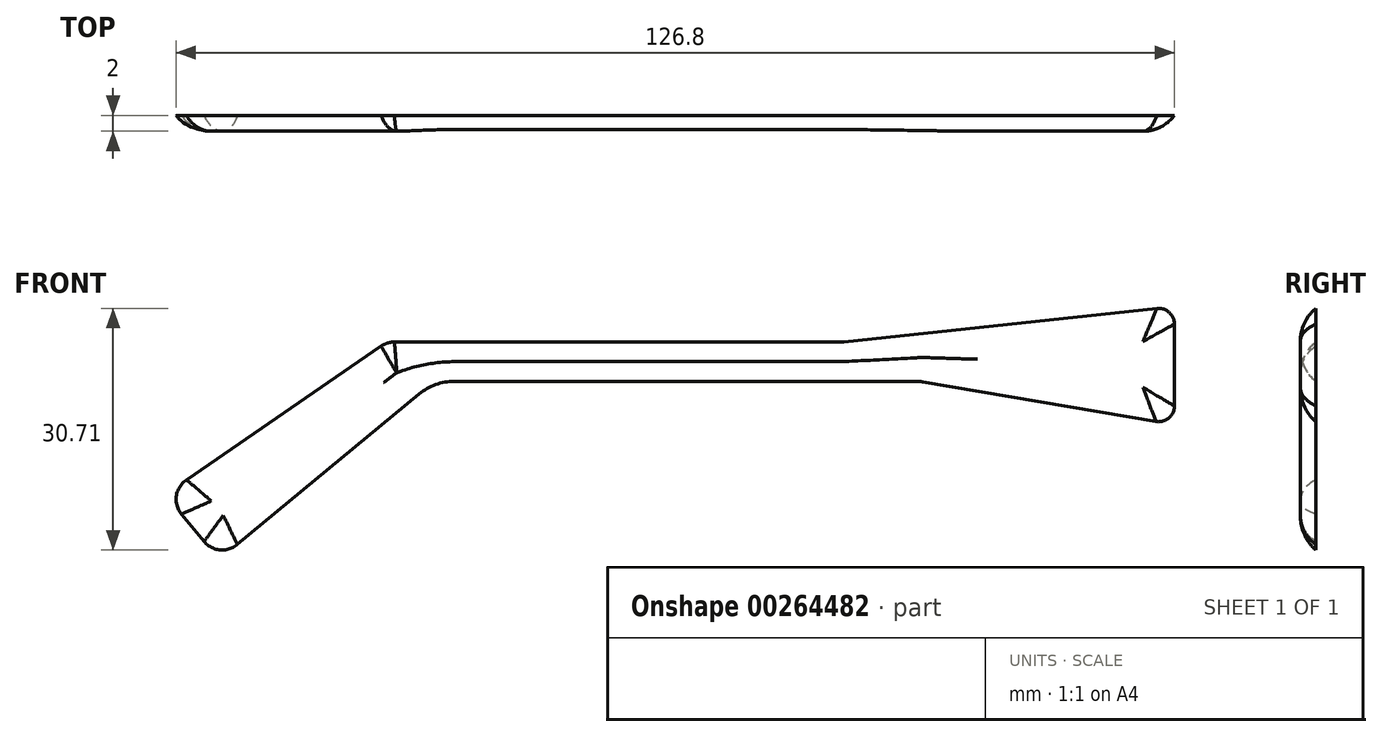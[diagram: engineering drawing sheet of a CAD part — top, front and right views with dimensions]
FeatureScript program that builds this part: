
annotation { "Feature Type Name" : "Feature", "Feature Type Description" : "" }
export const myFeature = defineFeature(function(context is Context, id is Id, definition is map)
    precondition{}
    {
        {
            var Q0;
            Q0=qCreatedBy(makeId("Front.planeOp"),FACE);
            var sketch = newSketch(context, id + "F0", { "sketchPlane" : qUnion([Q0])});
            skLineSegment(sketch, "E0", {"start": v(-40.92, 30.56) * mm, "end": v(15.64, 30.56) * mm});
            skLineSegment(sketch, "E1", {"start": v(16.17, 30.59) * mm, "end": v(55.94, 34.83) * mm});
            skLineSegment(sketch, "E2", {"start": v(58.15, 32.84) * mm, "end": v(58.15, 22.43) * mm});
            skLineSegment(sketch, "E3", {"start": v(55.82, 20.46) * mm, "end": v(26.24, 25.49) * mm});
            skLineSegment(sketch, "E4", {"start": v(25.4, 25.56) * mm, "end": v(-33.3, 25.56) * mm});
            skLineSegment(sketch, "E5", {"start": v(-37.77, 23.95) * mm, "end": v(-60.88, 4.82) * mm});
            skLineSegment(sketch, "E6", {"start": v(-65.1, 5.22) * mm, "end": v(-67.96, 8.67) * mm});
            skLineSegment(sketch, "E7", {"start": v(-67.35, 13.06) * mm, "end": v(-42.61, 30.03) * mm});
            skPoint(sketch, "E8.visualSharp", {"position": v(58.15, 35.06) * mm});
            skArc(sketch, "E8.filletArc", {"start": v(58.15, 32.84) * mm, "mid": v(57.5, 34.33) * mm, "end": v(55.94, 34.83) * mm});
            skPoint(sketch, "E9.visualSharp", {"position": v(58.15, 20.06) * mm});
            skArc(sketch, "E9.filletArc", {"start": v(55.82, 20.46) * mm, "mid": v(57.44, 20.9) * mm, "end": v(58.15, 22.43) * mm});
            skPoint(sketch, "E10.visualSharp", {"position": v(15.9, 30.56) * mm});
            skArc(sketch, "E10.filletArc", {"start": v(15.64, 30.56) * mm, "mid": v(15.9, 30.57) * mm, "end": v(16.17, 30.59) * mm});
            skPoint(sketch, "E11.visualSharp", {"position": v(25.83, 25.56) * mm});
            skArc(sketch, "E11.filletArc", {"start": v(26.24, 25.49) * mm, "mid": v(25.83, 25.54) * mm, "end": v(25.4, 25.56) * mm});
            skPoint(sketch, "E12.visualSharp", {"position": v(-70.06, 11.2) * mm});
            skArc(sketch, "E12.filletArc", {"start": v(-67.35, 13.06) * mm, "mid": v(-68.62, 11) * mm, "end": v(-67.96, 8.67) * mm});
            skPoint(sketch, "E13.visualSharp", {"position": v(-63.2, 2.91) * mm});
            skArc(sketch, "E13.filletArc", {"start": v(-65.1, 5.22) * mm, "mid": v(-63.08, 4.15) * mm, "end": v(-60.88, 4.82) * mm});
            skPoint(sketch, "E14.visualSharp", {"position": v(-41.85, 30.56) * mm});
            skArc(sketch, "E14.filletArc", {"start": v(-40.92, 30.56) * mm, "mid": v(-41.8, 30.42) * mm, "end": v(-42.61, 30.03) * mm});
            skPoint(sketch, "E15.visualSharp", {"position": v(-35.83, 25.56) * mm});
            skArc(sketch, "E15.filletArc", {"start": v(-33.3, 25.56) * mm, "mid": v(-35.68, 25.14) * mm, "end": v(-37.77, 23.95) * mm});
            skSolve(sketch);
        }
        {
            var Q0;
            Q0 = qSketchRegion(id + "F0", true);
            extrude(context, id + "F1", {"entities" : qUnion([Q0]), "depth" : 2 * mm});
        }
        {
            var Q0;
            Q0=makeQuery(id+"F1.opExtrude","CAP_EDGE",EDGE,{"disambiguationData":[OSD([sQuery(id+"F0.wireOp",EDGE,"E4")])],"isStart":false});
            fillet(context, id + "F2", {"entities" : qUnion([Q0]), "radius" : 5 * mm, "tangentPropagation" : true, "allowEdgeOverflow" : false});
        }
    });
